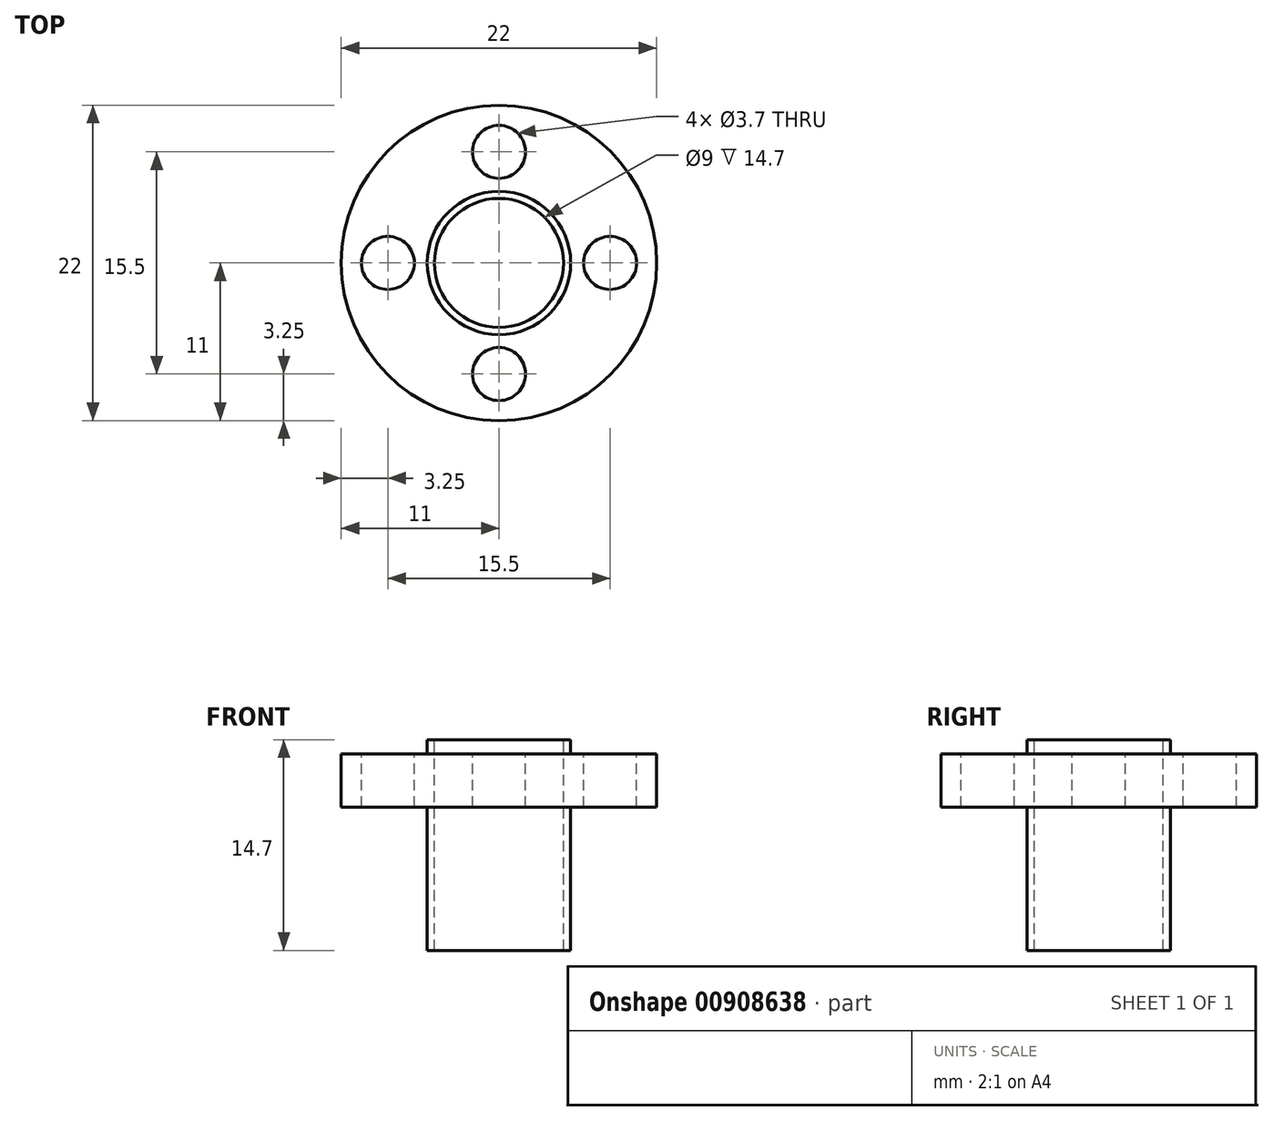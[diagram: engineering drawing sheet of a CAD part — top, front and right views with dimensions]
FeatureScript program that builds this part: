
annotation { "Feature Type Name" : "Feature", "Feature Type Description" : "" }
export const myFeature = defineFeature(function(context is Context, id is Id, definition is map)
    precondition{}
    {
        {
            var Q0;
            Q0=qCreatedBy(makeId("Top.planeOp"),FACE);
            var sketch = newSketch(context, id + "F0", { "sketchPlane" : qUnion([Q0])});
            skCircle(sketch, "E0", {"center": v(0, 0) * mm, "radius": 11 * mm});
            skSolve(sketch);
        }
        {
            var Q0;
            Q0 = qSketchRegion(id + "F0", true);
            extrude(context, id + "F1", {"entities" : qUnion([Q0]), "depth" : 3.7 * mm, "offsetDistance" : 25 * mm});
        }
        {
            var Q0;
            Q0=makeQuery(id+"F1.opExtrude","CAP_FACE",FACE,{"disambiguationData":[OSD([sQuery(id+"F0.wireOp",EDGE,"E0")])],"isStart":false});
            var sketch = newSketch(context, id + "F2", { "sketchPlane" : qUnion([Q0])});
            skCircle(sketch, "E1", {"center": v(0, 0) * mm, "radius": 5 * mm});
            skSolve(sketch);
        }
        {
            var Q0;
            Q0 = qSketchRegion(id + "F2", true);
            extrude(context, id + "F3", {"entities" : qUnion([Q0]), "operationType" : NewBodyOperationType.ADD, "depth" : 1 * mm, "offsetDistance" : 25 * mm});
        }
        {
            var Q0;
            Q0=makeQuery(id+"F1.opExtrude","CAP_FACE",FACE,{"disambiguationData":[OSD([sQuery(id+"F0.wireOp",EDGE,"E0")])],"isStart":true});
            var sketch = newSketch(context, id + "F4", { "sketchPlane" : qUnion([Q0])});
            skCircle(sketch, "E2", {"center": v(0, 0) * mm, "radius": 5 * mm});
            skSolve(sketch);
        }
        {
            var Q0;
            Q0 = qSketchRegion(id + "F4", true);
            extrude(context, id + "F5", {"entities" : qUnion([Q0]), "operationType" : NewBodyOperationType.ADD, "depth" : 10 * mm, "offsetDistance" : 25 * mm});
        }
        {
            var Q0;
            Q0=makeQuery(id+"F3.opExtrude","CAP_FACE",FACE,{"disambiguationData":[OSD([sQuery(id+"F2.wireOp",EDGE,"E1")])],"isStart":false});
            var sketch = newSketch(context, id + "F6", { "sketchPlane" : qUnion([Q0])});
            skCircle(sketch, "E3", {"center": v(0, 0) * mm, "radius": 4.5 * mm});
            skSolve(sketch);
        }
        {
            var Q0;
            Q0 = qSketchRegion(id + "F6", true);
            extrude(context, id + "F7", {"entities" : qUnion([Q0]), "operationType" : NewBodyOperationType.REMOVE, "endBound" : BoundingType.THROUGH_ALL, "oppositeDirection" : true, "depth" : 25 * mm, "offsetDistance" : 25 * mm});
        }
        {
            var Q0;
            Q0=makeQuery(id+"F1.opExtrude","CAP_FACE",FACE,{"disambiguationData":[OSD([sQuery(id+"F0.wireOp",EDGE,"E0")])],"isStart":false});
            var sketch = newSketch(context, id + "F8", { "sketchPlane" : qUnion([Q0])});
            skLineSegment(sketch, "E4", {"start": v(0, 0) * mm, "end": v(0, 11) * mm, "construction": true});
            skCircle(sketch, "E5", {"center": v(0, 7.75) * mm, "radius": 1.85 * mm});
            skCircle(sketch, "E6.1.0", {"center": v(-7.75, 0) * mm, "radius": 1.85 * mm});
            skCircle(sketch, "E6.2.0", {"center": v(0, -7.75) * mm, "radius": 1.85 * mm});
            skCircle(sketch, "E6.3.0", {"center": v(7.75, 0) * mm, "radius": 1.85 * mm});
            skPoint(sketch, "E6.center", {"position": v(0, 0) * mm});
            skSolve(sketch);
        }
        {
            var Q0;
            Q0 = qSketchRegion(id + "F8", true);
            extrude(context, id + "F9", {"entities" : qUnion([Q0]), "operationType" : NewBodyOperationType.REMOVE, "endBound" : BoundingType.THROUGH_ALL, "oppositeDirection" : true, "depth" : 25 * mm, "offsetDistance" : 25 * mm});
        }
    });
